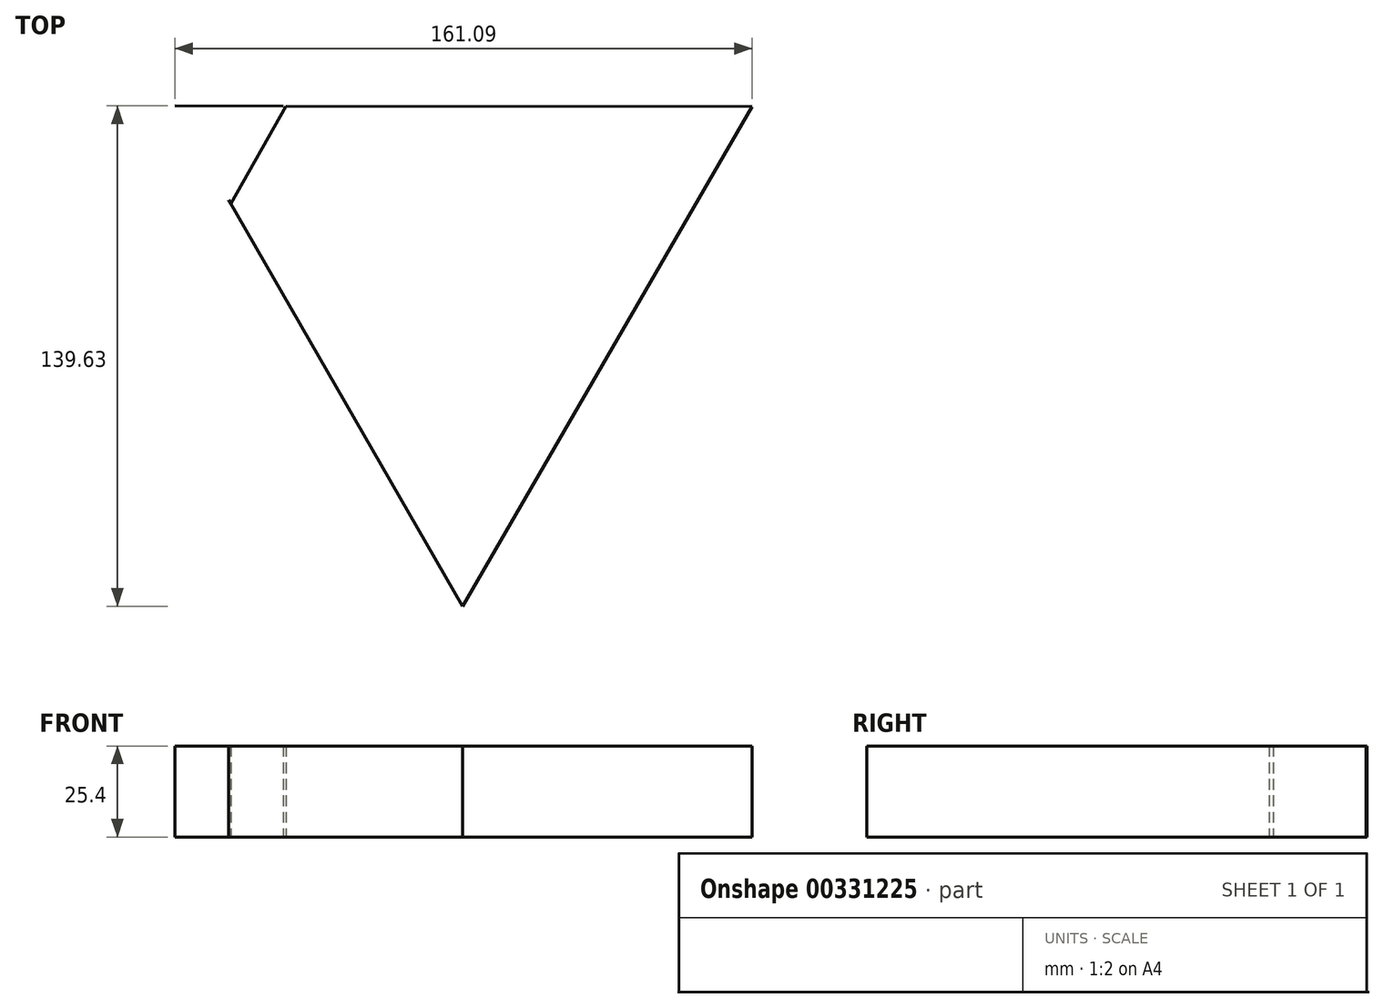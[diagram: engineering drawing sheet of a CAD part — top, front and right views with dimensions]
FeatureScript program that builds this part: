
annotation { "Feature Type Name" : "Feature", "Feature Type Description" : "" }
export const myFeature = defineFeature(function(context is Context, id is Id, definition is map)
    precondition{}
    {
        {
            var Q0;
            Q0=qCreatedBy(makeId("Top.planeOp"),FACE);
            var sketch = newSketch(context, id + "F0", { "sketchPlane" : qUnion([Q0])});
            skCircle(sketch, "E0.cCircle", {"center": v(0, 0) * mm, "radius": 46.5 * mm, "construction": true});
            skLineSegment(sketch, "E0.0", {"start": v(80.62, 46.37) * mm, "end": v(-0.15, -93) * mm});
            skLineSegment(sketch, "E0.1", {"start": v(-0.15, -93) * mm, "end": v(-80.47, 46.63) * mm});
            skLineSegment(sketch, "E0.2", {"start": v(-80.47, 46.63) * mm, "end": v(80.62, 46.37) * mm});
            skPoint(sketch, "E0.0.midPoint", {"position": v(40.23, -23.32) * mm});
            skSolve(sketch);
        }
        {
            var Q0;
            Q0=makeQuery(id+"F0.imprint","IMPRINT",FACE,{"disambiguationData":[TD([[makeQuery(id+"F0.imprint","IMPRINT",EDGE,{"derivedFrom":sQuery(id+"F0.wireOp",EDGE,"E0.0")}),-1.0]])]});
            var sketch = newSketch(context, id + "F1", { "sketchPlane" : qUnion([Q0])});
            skLineSegment(sketch, "E1", {"start": v(-49.4, 46.58) * mm, "end": v(-64.76, 19.33) * mm});
            skPoint(sketch, "E2", {"position": v(-64.76, 19.33) * mm});
            skPoint(sketch, "E3", {"position": v(-49.4, 46.58) * mm});
            skPoint(sketch, "E4", {"position": v(-80.58, 46.62) * mm});
            skLineSegment(sketch, "E5", {"start": v(-80.58, 46.62) * mm, "end": v(-64.76, 19.33) * mm});
            skLineSegment(sketch, "E6", {"start": v(-49.4, 46.58) * mm, "end": v(-80.58, 46.62) * mm});
            skSolve(sketch);
        }
        {
            var Q0;
            Q0 = qSketchRegion(id + "F0", true);
            extrude(context, id + "F2", {"entities" : qUnion([Q0]), "depth" : 25.4 * mm});
        }
        {
            var Q0;
            Q0 = qSketchRegion(id + "F1", true);
            extrude(context, id + "F3", {"entities" : qUnion([Q0]), "operationType" : NewBodyOperationType.REMOVE, "depth" : 25.4 * mm});
        }
    });
